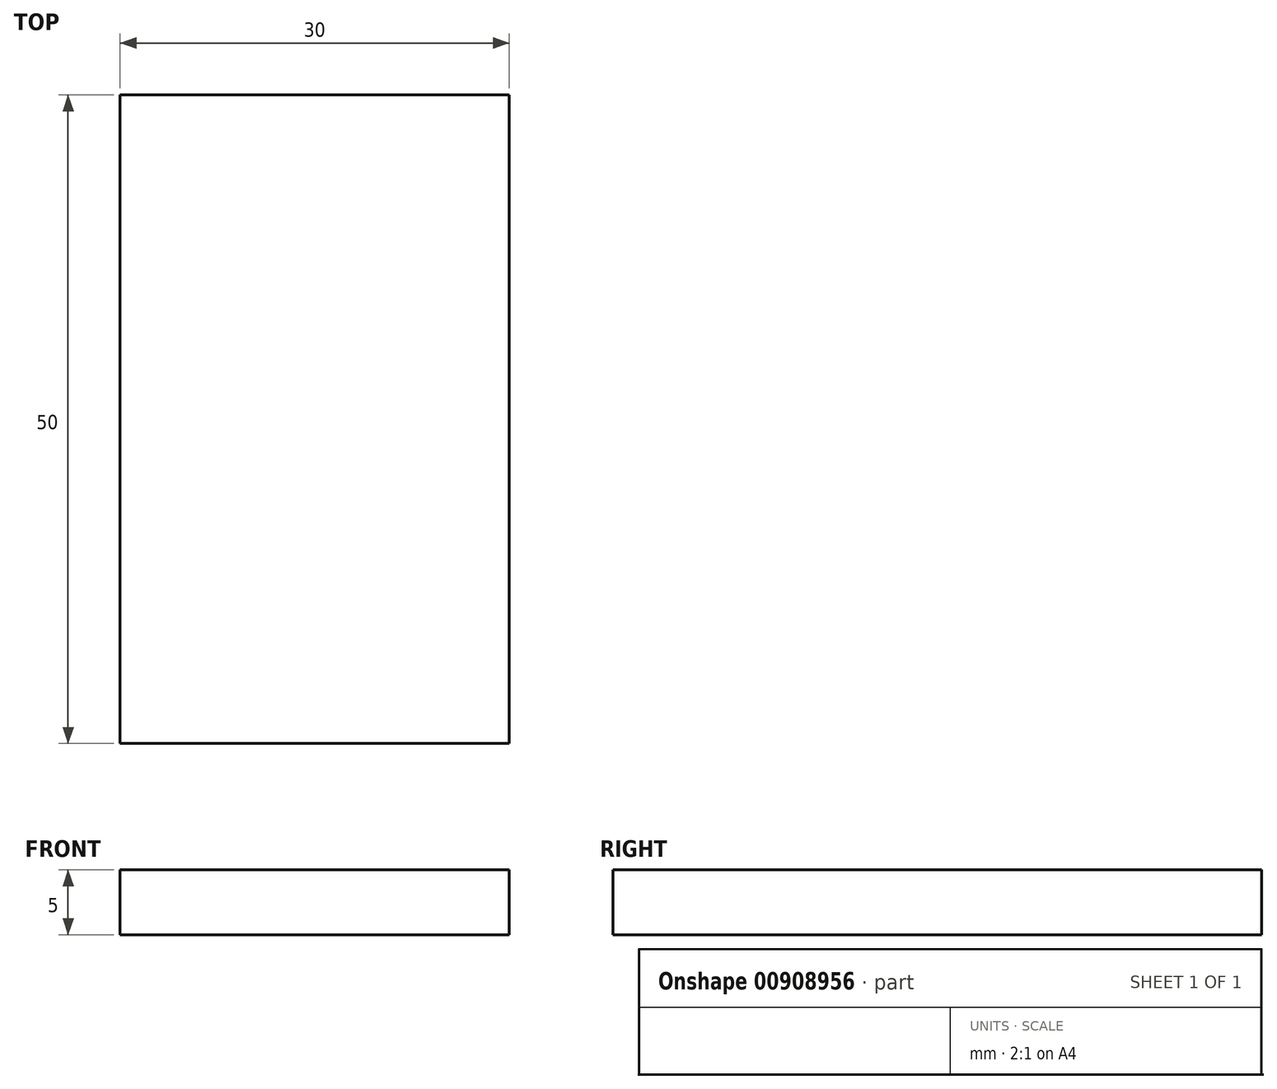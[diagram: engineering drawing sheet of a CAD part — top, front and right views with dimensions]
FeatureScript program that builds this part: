
annotation { "Feature Type Name" : "Feature", "Feature Type Description" : "" }
export const myFeature = defineFeature(function(context is Context, id is Id, definition is map)
    precondition{}
    {
        {
            var Q0;
            Q0=qCreatedBy(makeId("Top.planeOp"),FACE);
            var sketch = newSketch(context, id + "F0", { "sketchPlane" : qUnion([Q0])});
            skLineSegment(sketch, "E0.bottom", {"start": v(-80, -56.27) * mm, "end": v(-50, -56.27) * mm});
            skLineSegment(sketch, "E0.top", {"start": v(-80, -106.27) * mm, "end": v(-50, -106.27) * mm});
            skLineSegment(sketch, "E0.left", {"start": v(-80, -56.27) * mm, "end": v(-80, -106.27) * mm});
            skLineSegment(sketch, "E0.right", {"start": v(-50, -56.27) * mm, "end": v(-50, -106.27) * mm});
            skSolve(sketch);
        }
        {
            var Q0;
            Q0 = qSketchRegion(id + "F0", true);
            extrude(context, id + "F1", {"entities" : qUnion([Q0]), "depth" : 5 * mm, "offsetDistance" : 25 * mm});
        }
    });
